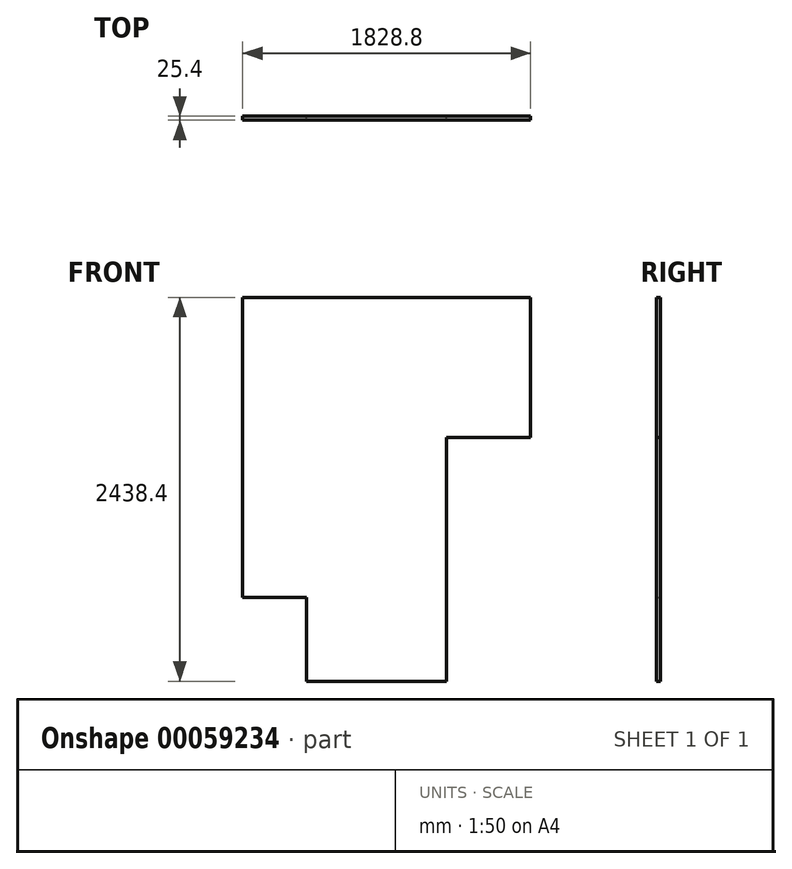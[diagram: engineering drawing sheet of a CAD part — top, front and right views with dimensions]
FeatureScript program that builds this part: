
annotation { "Feature Type Name" : "Feature", "Feature Type Description" : "" }
export const myFeature = defineFeature(function(context is Context, id is Id, definition is map)
    precondition{}
    {
        {
            var Q0;
            Q0=qCreatedBy(makeId("Front.planeOp"),FACE);
            var sketch = newSketch(context, id + "F0", { "sketchPlane" : qUnion([Q0])});
            skLineSegment(sketch, "E0", {"start": v(0, 0) * mm, "end": v(1828.8, 0) * mm});
            skLineSegment(sketch, "E1", {"start": v(1828.8, 0) * mm, "end": v(1828.8, -889) * mm});
            skLineSegment(sketch, "E2", {"start": v(1828.8, -889) * mm, "end": v(1295.4, -889) * mm});
            skLineSegment(sketch, "E3", {"start": v(1295.4, -889) * mm, "end": v(1295.4, -2438.4) * mm});
            skLineSegment(sketch, "E4", {"start": v(1295.4, -2438.4) * mm, "end": v(406.4, -2438.4) * mm});
            skLineSegment(sketch, "E5", {"start": v(406.4, -2438.4) * mm, "end": v(406.4, -1905) * mm});
            skLineSegment(sketch, "E6", {"start": v(406.4, -1905) * mm, "end": v(0, -1905) * mm});
            skLineSegment(sketch, "E7", {"start": v(0, -1905) * mm, "end": v(0, 0) * mm});
            skSolve(sketch);
        }
        {
            var Q0;
            Q0=makeQuery(id+"F0.imprint","IMPRINT",FACE,{"disambiguationData":[TD([[makeQuery(id+"F0.imprint","IMPRINT",EDGE,{"derivedFrom":sQuery(id+"F0.wireOp",EDGE,"E0")}),-1.0]])]});
            extrude(context, id + "F1", {"entities" : qUnion([Q0]), "depth" : 25.4 * mm});
        }
    });
